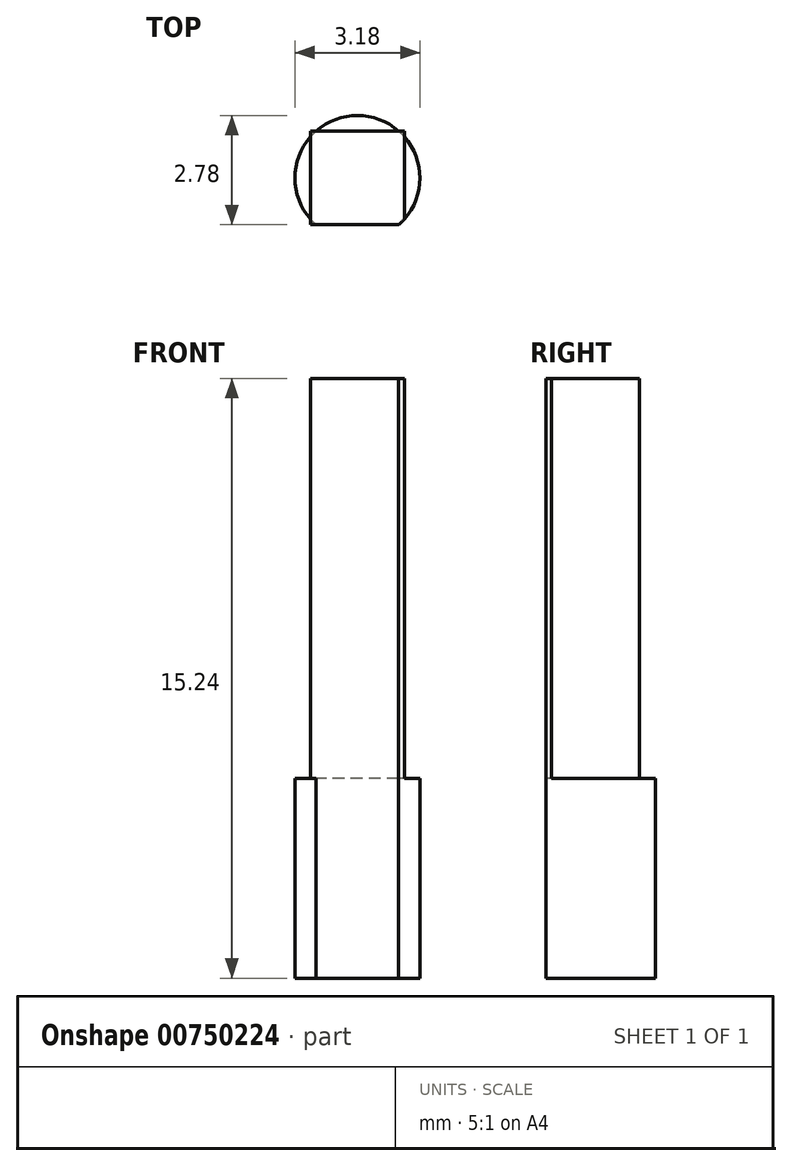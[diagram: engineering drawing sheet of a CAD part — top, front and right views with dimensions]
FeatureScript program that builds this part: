
annotation { "Feature Type Name" : "Feature", "Feature Type Description" : "" }
export const myFeature = defineFeature(function(context is Context, id is Id, definition is map)
    precondition{}
    {
        {
            var Q0;
            Q0=qCreatedBy(makeId("Top.planeOp"),FACE);
            var sketch = newSketch(context, id + "F0", { "sketchPlane" : qUnion([Q0])});
            skCircle(sketch, "E0", {"center": v(0, 0) * mm, "radius": 1.59 * mm});
            skLineSegment(sketch, "E1.bottom", {"start": v(1.2, 1.2) * mm, "end": v(-1.2, 1.2) * mm});
            skLineSegment(sketch, "E1.top", {"start": v(1.2, -1.2) * mm, "end": v(-1.2, -1.2) * mm});
            skLineSegment(sketch, "E1.left", {"start": v(1.2, 1.2) * mm, "end": v(1.2, -1.2) * mm});
            skLineSegment(sketch, "E1.right", {"start": v(-1.2, 1.2) * mm, "end": v(-1.2, -1.2) * mm});
            skSolve(sketch);
        }
        {
            var Q0;
            {var subQ0=sQuery(id+"F0.wireOp",EDGE,"E1.right");var subQ1=sQuery(id+"F0.wireOp",EDGE,"E0");var subQ2=makeQuery(id+"F0.imprint","INTERSECT",VERTEX,{"disambiguationData":[OD(1.0)],"derivedFrom":[subQ1,subQ0]});Q0=makeQuery(id+"F0.imprint","IMPRINT",FACE,{"disambiguationData":[TD([[makeQuery(id+"F0.imprint","IMPRINT",EDGE,{"disambiguationData":[TD([[subQ2,-1.0]])],"derivedFrom":subQ1}),-1.0]])]});}
            var Q1;
            {var subQ1=sQuery(id+"F0.wireOp",EDGE,"E0");var subQ9=sQuery(id+"F0.wireOp",EDGE,"E1.bottom");var subQ12=makeQuery(id+"F0.imprint","INTERSECT",VERTEX,{"disambiguationData":[OD(0.0)],"derivedFrom":[subQ1,subQ9]});Q1=makeQuery(id+"F0.imprint","IMPRINT",FACE,{"disambiguationData":[TD([[makeQuery(id+"F0.imprint","IMPRINT",EDGE,{"disambiguationData":[TD([[subQ12,1.0]])],"derivedFrom":subQ1}),1.0]])]});}
            var Q2;
            {var subQ0=sQuery(id+"F0.wireOp",EDGE,"E1.bottom");var subQ1=sQuery(id+"F0.wireOp",EDGE,"E0");var subQ2=makeQuery(id+"F0.imprint","INTERSECT",VERTEX,{"disambiguationData":[OD(1.0)],"derivedFrom":[subQ1,subQ0]});Q2=makeQuery(id+"F0.imprint","IMPRINT",FACE,{"disambiguationData":[TD([[makeQuery(id+"F0.imprint","IMPRINT",EDGE,{"disambiguationData":[TD([[subQ2,-1.0]])],"derivedFrom":subQ1}),-1.0]])]});}
            var Q3;
            {var subQ0=sQuery(id+"F0.wireOp",EDGE,"E1.bottom");var subQ1=sQuery(id+"F0.wireOp",EDGE,"E0");var subQ2=makeQuery(id+"F0.imprint","INTERSECT",VERTEX,{"disambiguationData":[OD(0.0)],"derivedFrom":[subQ1,subQ0]});Q3=makeQuery(id+"F0.imprint","IMPRINT",FACE,{"disambiguationData":[TD([[makeQuery(id+"F0.imprint","IMPRINT",EDGE,{"disambiguationData":[TD([[subQ2,1.0]])],"derivedFrom":subQ1}),-1.0]])]});}
            var Q4;
            {var subQ0=sQuery(id+"F0.wireOp",EDGE,"E1.top");var subQ1=sQuery(id+"F0.wireOp",EDGE,"E0");var subQ2=makeQuery(id+"F0.imprint","INTERSECT",VERTEX,{"disambiguationData":[OD(1.0)],"derivedFrom":[subQ1,subQ0]});Q4=makeQuery(id+"F0.imprint","IMPRINT",FACE,{"disambiguationData":[TD([[makeQuery(id+"F0.imprint","IMPRINT",EDGE,{"disambiguationData":[TD([[subQ2,-1.0]])],"derivedFrom":subQ1}),-1.0]])]});}
            extrude(context, id + "F1", {"entities" : qUnion([Q0, Q1, Q2, Q3, Q4]), "depth" : 10.16 * mm, "offsetDistance" : 25.4 * mm});
        }
        {
            var Q0;
            {var subQ0=sQuery(id+"F0.wireOp",EDGE,"E1.top");var subQ1=sQuery(id+"F0.wireOp",EDGE,"E0");var subQ2=makeQuery(id+"F0.imprint","INTERSECT",VERTEX,{"disambiguationData":[OD(0.0)],"derivedFrom":[subQ1,subQ0]});Q0=makeQuery(id+"F0.imprint","IMPRINT",FACE,{"disambiguationData":[TD([[makeQuery(id+"F0.imprint","IMPRINT",EDGE,{"disambiguationData":[TD([[subQ2,-1.0]])],"derivedFrom":subQ1}),1.0]])]});}
            var Q1;
            {var subQ0=sQuery(id+"F0.wireOp",EDGE,"E1.right");var subQ1=sQuery(id+"F0.wireOp",EDGE,"E0");var subQ2=makeQuery(id+"F0.imprint","INTERSECT",VERTEX,{"disambiguationData":[OD(0.0)],"derivedFrom":[subQ1,subQ0]});Q1=makeQuery(id+"F0.imprint","IMPRINT",FACE,{"disambiguationData":[TD([[makeQuery(id+"F0.imprint","IMPRINT",EDGE,{"disambiguationData":[TD([[subQ2,-1.0]])],"derivedFrom":subQ1}),1.0]])]});}
            var Q2;
            {var subQ1=sQuery(id+"F0.wireOp",EDGE,"E0");var subQ9=sQuery(id+"F0.wireOp",EDGE,"E1.bottom");var subQ12=makeQuery(id+"F0.imprint","INTERSECT",VERTEX,{"disambiguationData":[OD(0.0)],"derivedFrom":[subQ1,subQ9]});Q2=makeQuery(id+"F0.imprint","IMPRINT",FACE,{"disambiguationData":[TD([[makeQuery(id+"F0.imprint","IMPRINT",EDGE,{"disambiguationData":[TD([[subQ12,1.0]])],"derivedFrom":subQ1}),1.0]])]});}
            var Q3;
            {var subQ0=sQuery(id+"F0.wireOp",EDGE,"E1.bottom");var subQ1=sQuery(id+"F0.wireOp",EDGE,"E0");var subQ2=makeQuery(id+"F0.imprint","INTERSECT",VERTEX,{"disambiguationData":[OD(0.0)],"derivedFrom":[subQ1,subQ0]});Q3=makeQuery(id+"F0.imprint","IMPRINT",FACE,{"disambiguationData":[TD([[makeQuery(id+"F0.imprint","IMPRINT",EDGE,{"disambiguationData":[TD([[subQ2,-1.0]])],"derivedFrom":subQ1}),1.0]])]});}
            var Q4;
            {var subQ0=sQuery(id+"F0.wireOp",EDGE,"E1.left");var subQ1=sQuery(id+"F0.wireOp",EDGE,"E0");var subQ2=makeQuery(id+"F0.imprint","INTERSECT",VERTEX,{"disambiguationData":[OD(0.0)],"derivedFrom":[subQ1,subQ0]});Q4=makeQuery(id+"F0.imprint","IMPRINT",FACE,{"disambiguationData":[TD([[makeQuery(id+"F0.imprint","IMPRINT",EDGE,{"disambiguationData":[TD([[subQ2,1.0]])],"derivedFrom":subQ1}),1.0]])]});}
            extrude(context, id + "F2", {"entities" : qUnion([Q0, Q1, Q2, Q3, Q4]), "operationType" : NewBodyOperationType.ADD, "oppositeDirection" : true, "depth" : 5.08 * mm, "offsetDistance" : 25.4 * mm});
        }
    });
